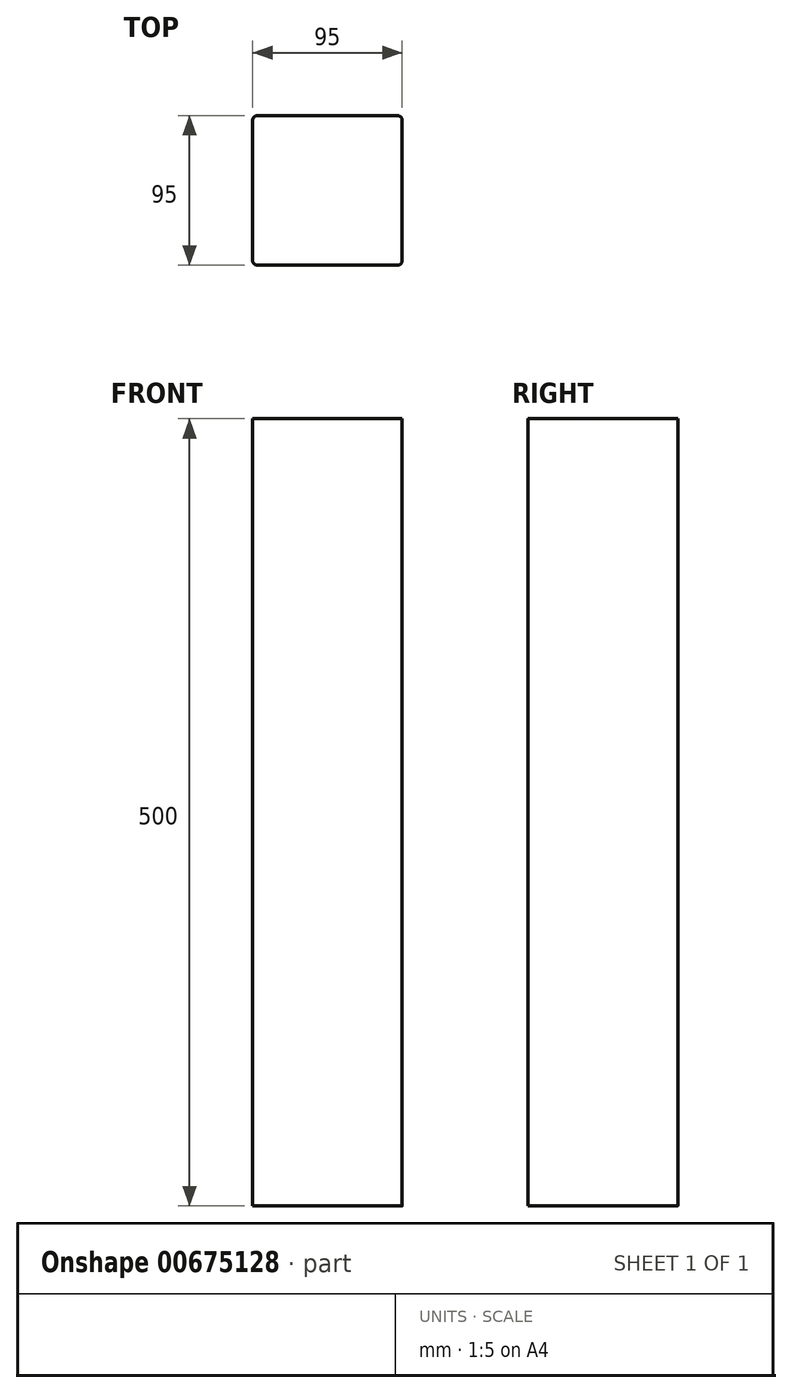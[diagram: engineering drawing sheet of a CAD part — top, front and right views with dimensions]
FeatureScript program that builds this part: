
annotation { "Feature Type Name" : "Feature", "Feature Type Description" : "" }
export const myFeature = defineFeature(function(context is Context, id is Id, definition is map)
    precondition{}
    {
        {
            var Q0;
            Q0=qCreatedBy(makeId("Top.planeOp"),FACE);
            var sketch = newSketch(context, id + "F0", { "sketchPlane" : qUnion([Q0])});
            skLineSegment(sketch, "E0.bottom", {"start": v(3, 0) * mm, "end": v(92, 0) * mm});
            skLineSegment(sketch, "E0.top", {"start": v(3, 95) * mm, "end": v(92, 95) * mm});
            skLineSegment(sketch, "E0.left", {"start": v(0, 3) * mm, "end": v(0, 92) * mm});
            skLineSegment(sketch, "E0.right", {"start": v(95, 3) * mm, "end": v(95, 92) * mm});
            skPoint(sketch, "E1.visualSharp", {"position": v(0, 0) * mm});
            skArc(sketch, "E1.filletArc", {"start": v(0, 3) * mm, "mid": v(0.88, 0.88) * mm, "end": v(3, 0) * mm});
            skPoint(sketch, "E2.visualSharp", {"position": v(0, 95) * mm});
            skArc(sketch, "E2.filletArc", {"start": v(3, 95) * mm, "mid": v(0.88, 94.12) * mm, "end": v(0, 92) * mm});
            skPoint(sketch, "E3.visualSharp", {"position": v(95, 95) * mm});
            skArc(sketch, "E3.filletArc", {"start": v(95, 92) * mm, "mid": v(94.12, 94.12) * mm, "end": v(92, 95) * mm});
            skPoint(sketch, "E4.visualSharp", {"position": v(95, 0) * mm});
            skArc(sketch, "E4.filletArc", {"start": v(92, 0) * mm, "mid": v(94.12, 0.88) * mm, "end": v(95, 3) * mm});
            skSolve(sketch);
        }
        {
            var Q0;
            Q0 = qSketchRegion(id + "F0", true);
            extrude(context, id + "F1", {"entities" : qUnion([Q0]), "depth" : 500 * mm, "offsetDistance" : 25 * mm});
        }
    });
